# Revit family: 931-20-001 DN500-600
name_source: partatom
category: Pipe Accessories
units: mm (PartAtom-declared; Revit-internal decimal feet)

## family parameters
Always vertical = Yes
Cut with Voids When Loaded = No
Part Type = Valve - Breaks Into
Round Connector Dimension = Use Diameter
Shared = No
Work Plane-Based = No

## types (4) — shared parameters
1 = 1 mm  [stored 0.00328084 ft]
2 = 3 mm  [stored 0.00984252 ft]
Body_Thickness = 2 mm  [stored 0.00656168 ft]
DN500_PN10 = 931-500-20-010020200000
DN500_PN16 = 931-500-20-020020200000
DN600_PN10 = 931-600-20-010020200000
DN600_PN16 = 931-600-20-020020200000
Description_ = AVK BUTTERFLY VALVE, LUG, PN10/16
H = 105 mm  [stored 0.344488 ft]
Search_table = 931-20-001 DN500-600
URL_product_pages = https://www.avkvalves.com
wafer_F = 41 mm  [stored 0.134514 ft]
zero-valued in all types: DISK, Default Elevation

## per-type parameters (varying)
- DN600_PN10: Actuator_FL_T=30 mm  [stored 0.0984252 ft]; Actuator_Flange_R=105 mm  [stored 0.344488 ft]; B=289 mm; B1=290 mm; Body_dim=53 mm; Body_dim1=108 mm; Body_thickness=304 mm; Bore_R=300 mm; C=154 mm  [stored 0.505249 ft]; D=359 mm; DN=600 mm; E=495 mm; F=68 mm  [stored 0.223097 ft]; Flange_R=350 mm; Flange_T=30 mm  [stored 0.0984252 ft]; G=46 mm  [stored 0.150919 ft]; Hole=51 mm; Hole1=25 mm  [stored 0.082021 ft]; PCD_R=363 mm; Slot_dim=35 mm  [stored 0.114829 ft]; base=54 mm; base1=31 mm  [stored 0.101706 ft]; base_dis=423 mm; disk=25 mm  [stored 0.082021 ft]; disk1=44 mm  [stored 0.144357 ft]; disk11=57 mm  [stored 0.187008 ft]; disk2=577 mm; disk22=33 mm; hole1=23 mm  [stored 0.0754593 ft]; rubber=29 mm  [stored 0.0951444 ft]; support=432 mm; wafer=158 mm; wafer_dim1=30 mm  [stored 0.0984252 ft]; wafer_dim2=158 mm; wafer_fillet=79 mm
- DN500_PN10: Actuator_FL_T=20 mm  [stored 0.0656168 ft]; Actuator_Flange_R=88 mm; B=246 mm  [stored 0.807087 ft]; B1=247 mm; Body_dim=44 mm  [stored 0.144357 ft]; Body_dim1=89 mm; Body_thickness=259 mm; Bore_R=250 mm; C=127 mm; D=299 mm; DN=500 mm; E=403 mm; F=39 mm  [stored 0.127953 ft]; Flange_R=285 mm; Flange_T=27 mm  [stored 0.0885827 ft]; G=36 mm  [stored 0.11811 ft]; Hole=40 mm  [stored 0.131234 ft]; Hole1=18 mm  [stored 0.0590551 ft]; PCD_R=310 mm; Slot_dim=29 mm  [stored 0.0951444 ft]; base=44 mm  [stored 0.144357 ft]; base1=25 mm  [stored 0.082021 ft]; base_dis=352 mm; disk=20 mm  [stored 0.0656168 ft]; disk1=34 mm  [stored 0.111549 ft]; disk11=44 mm  [stored 0.144357 ft]; disk2=492 mm; disk22=26 mm; hole1=18 mm  [stored 0.0590551 ft]; rubber=24 mm  [stored 0.0787402 ft]; support=349 mm; wafer=131 mm; wafer_dim1=27 mm  [stored 0.0885827 ft]; wafer_dim2=131 mm; wafer_fillet=66 mm
- DN600_PN16: Actuator_FL_T=30 mm  [stored 0.0984252 ft]; Actuator_Flange_R=105 mm  [stored 0.344488 ft]; B=289 mm; B1=290 mm; Body_dim=53 mm; Body_dim1=108 mm; Body_thickness=304 mm; Bore_R=300 mm; C=154 mm  [stored 0.505249 ft]; D=359 mm; DN=600 mm; E=495 mm; F=68 mm  [stored 0.223097 ft]; Flange_R=350 mm; Flange_T=36 mm  [stored 0.11811 ft]; G=46 mm  [stored 0.150919 ft]; Hole=51 mm; Hole1=25 mm  [stored 0.082021 ft]; PCD_R=385 mm; Slot_dim=35 mm  [stored 0.114829 ft]; base=54 mm; base1=31 mm  [stored 0.101706 ft]; base_dis=423 mm; disk=25 mm  [stored 0.082021 ft]; disk1=44 mm  [stored 0.144357 ft]; disk11=57 mm  [stored 0.187008 ft]; disk2=577 mm; disk22=33 mm; hole1=23 mm  [stored 0.0754593 ft]; rubber=29 mm  [stored 0.0951444 ft]; support=432 mm; wafer=158 mm; wafer_dim1=36 mm  [stored 0.11811 ft]; wafer_dim2=158 mm; wafer_fillet=79 mm
- DN500_PN16: Actuator_FL_T=18 mm  [stored 0.0590551 ft]; Actuator_Flange_R=88 mm; B=246 mm  [stored 0.807087 ft]; B1=247 mm; Body_dim=44 mm  [stored 0.144357 ft]; Body_dim1=89 mm; Body_thickness=259 mm; Bore_R=250 mm; C=127 mm; D=299 mm; DN=500 mm; E=403 mm; F=39 mm  [stored 0.127953 ft]; Flange_R=300 mm; Flange_T=32 mm  [stored 0.104987 ft]; G=36 mm  [stored 0.11811 ft]; Hole=40 mm  [stored 0.131234 ft]; Hole1=18 mm  [stored 0.0590551 ft]; PCD_R=325 mm; Slot_dim=29 mm  [stored 0.0951444 ft]; base=44 mm  [stored 0.144357 ft]; base1=25 mm  [stored 0.082021 ft]; base_dis=352 mm; disk=20 mm  [stored 0.0656168 ft]; disk1=34 mm  [stored 0.111549 ft]; disk11=44 mm  [stored 0.144357 ft]; disk2=492 mm; disk22=26 mm; hole1=18 mm  [stored 0.0590551 ft]; rubber=24 mm  [stored 0.0787402 ft]; support=349 mm; wafer=131 mm; wafer_dim1=32 mm  [stored 0.104987 ft]; wafer_dim2=131 mm; wafer_fillet=66 mm

note: [stored X ft] marks values corroborated as IEEE doubles in the binary element streams (Revit-internal decimal feet)

## geometry (parser evidence)
native form markers: Sweep x4
no freeform markers — native parametric forms only
